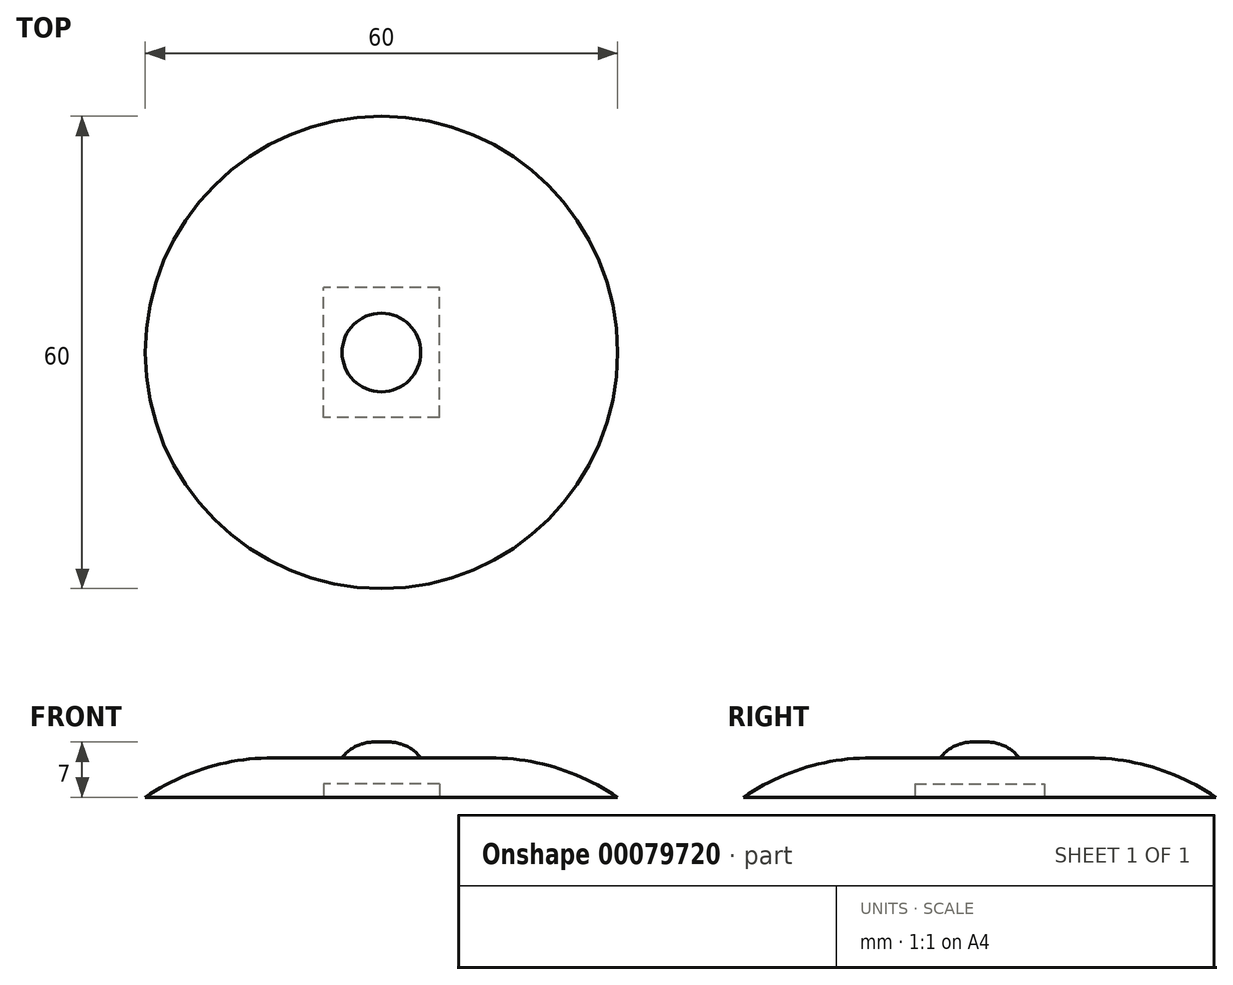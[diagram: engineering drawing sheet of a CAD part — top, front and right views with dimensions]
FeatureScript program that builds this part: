
annotation { "Feature Type Name" : "Feature", "Feature Type Description" : "" }
export const myFeature = defineFeature(function(context is Context, id is Id, definition is map)
    precondition{}
    {
        {
            var Q0;
            Q0=qCreatedBy(makeId("Top.planeOp"),FACE);
            var sketch = newSketch(context, id + "F0", { "sketchPlane" : qUnion([Q0])});
            skCircle(sketch, "E0", {"center": v(0, 0) * mm, "radius": 30 * mm});
            skSolve(sketch);
        }
        {
            var Q0;
            Q0 = qSketchRegion(id + "F0", true);
            extrude(context, id + "F1", {"entities" : qUnion([Q0]), "depth" : 5 * mm});
        }
        {
            var Q0;
            Q0=makeQuery(id+"F1.opExtrude","CAP_EDGE",EDGE,{"disambiguationData":[OSD([sQuery(id+"F0.wireOp",EDGE,"E0")])],"isStart":false});
            fillet(context, id + "F2", {"entities" : qUnion([Q0]), "radius" : 28.76 * mm, "tangentPropagation" : true, "allowEdgeOverflow" : false});
        }
        {
            var Q0;
            Q0=makeQuery(id+"F1.opExtrude","CAP_FACE",FACE,{"disambiguationData":[OSD([sQuery(id+"F0.wireOp",EDGE,"E0")])],"isStart":false});
            var sketch = newSketch(context, id + "F3", { "sketchPlane" : qUnion([Q0])});
            skCircle(sketch, "E1", {"center": v(0, 0) * mm, "radius": 5 * mm});
            skSolve(sketch);
        }
        {
            var Q0;
            Q0 = qSketchRegion(id + "F3", true);
            extrude(context, id + "F4", {"entities" : qUnion([Q0]), "operationType" : NewBodyOperationType.ADD, "depth" : 2 * mm});
        }
        {
            var Q0;
            Q0=makeQuery(id+"F1.opExtrude","CAP_FACE",FACE,{"disambiguationData":[OSD([sQuery(id+"F0.wireOp",EDGE,"E0")])],"isStart":true});
            var sketch = newSketch(context, id + "F5", { "sketchPlane" : qUnion([Q0])});
            skLineSegment(sketch, "E2.bottom", {"start": v(7.35, 8.25) * mm, "end": v(-7.35, 8.25) * mm});
            skLineSegment(sketch, "E2.top", {"start": v(7.35, -8.25) * mm, "end": v(-7.35, -8.25) * mm});
            skLineSegment(sketch, "E2.left", {"start": v(7.35, 8.25) * mm, "end": v(7.35, -8.25) * mm});
            skLineSegment(sketch, "E2.right", {"start": v(-7.35, 8.25) * mm, "end": v(-7.35, -8.25) * mm});
            skPoint(sketch, "E2.middle", {"position": v(0, 0) * mm});
            skSolve(sketch);
        }
        {
            var Q0;
            Q0=makeQuery(id+"F5.imprint","IMPRINT",FACE,{"disambiguationData":[TD([[makeQuery(id+"F5.imprint","IMPRINT",EDGE,{"derivedFrom":sQuery(id+"F5.wireOp",EDGE,"E2.bottom")}),1.0]])]});
            extrude(context, id + "F6", {"entities" : qUnion([Q0]), "operationType" : NewBodyOperationType.REMOVE, "oppositeDirection" : true, "depth" : 1.7 * mm});
        }
        {
            var Q0;
            Q0=makeQuery(id+"F4.opExtrude","CAP_FACE",FACE,{"disambiguationData":[OSD([sQuery(id+"F3.wireOp",EDGE,"E1")])],"isStart":false});
            fillet(context, id + "F7", {"entities" : qUnion([Q0]), "radius" : 5 * mm, "tangentPropagation" : true, "allowEdgeOverflow" : false});
        }
    });
